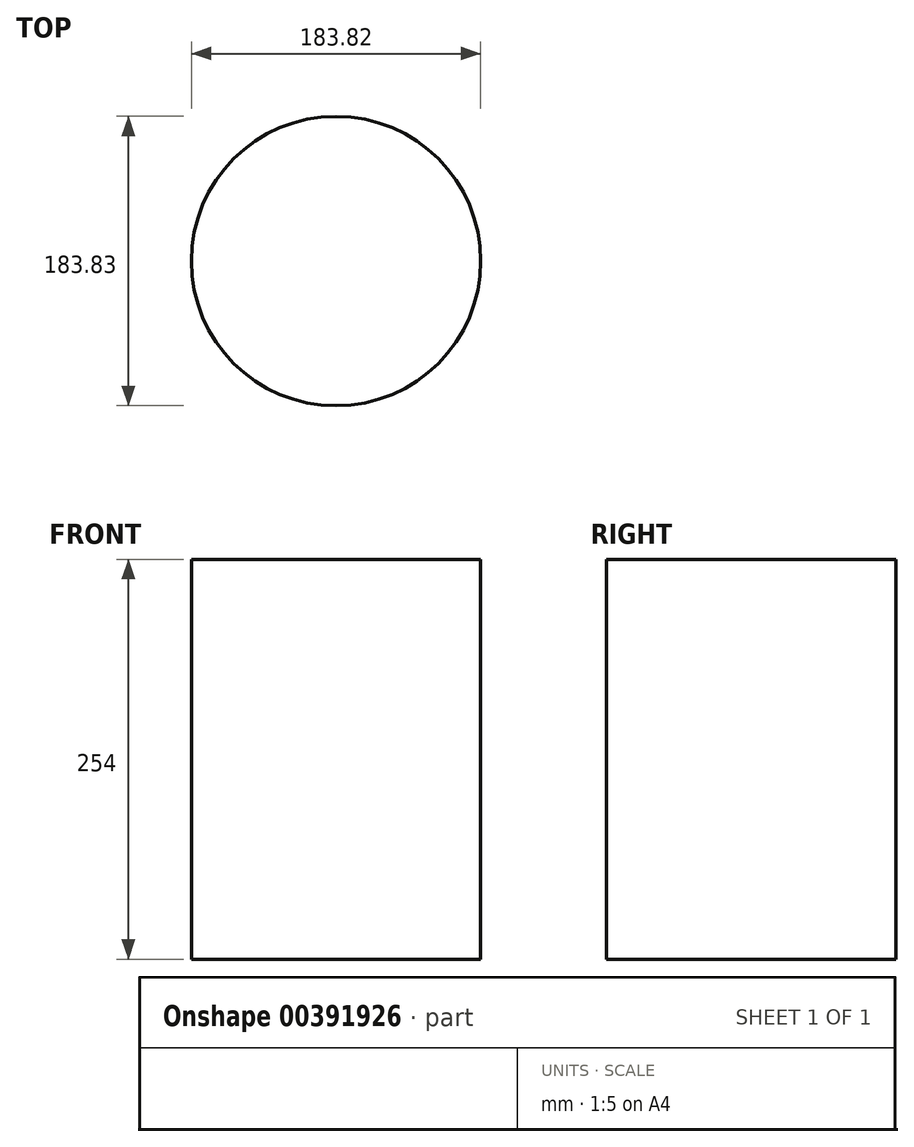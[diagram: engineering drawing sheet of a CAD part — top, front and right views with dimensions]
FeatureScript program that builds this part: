
annotation { "Feature Type Name" : "Feature", "Feature Type Description" : "" }
export const myFeature = defineFeature(function(context is Context, id is Id, definition is map)
    precondition{}
    {
        {
            var Q0;
            Q0=qCreatedBy(makeId("Top.planeOp"),FACE);
            var sketch = newSketch(context, id + "F0", { "sketchPlane" : qUnion([Q0])});
            skCircle(sketch, "E0", {"center": v(-35.64, 35.92) * mm, "radius": 91.91 * mm});
            skSolve(sketch);
        }
        {
            var Q0;
            Q0 = qSketchRegion(id + "F0", true);
            extrude(context, id + "F1", {"entities" : qUnion([Q0]), "depth" : 254 * mm});
        }
    });
